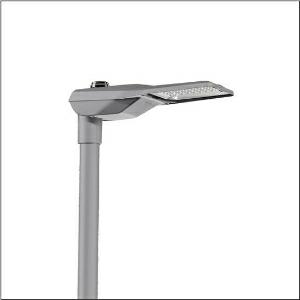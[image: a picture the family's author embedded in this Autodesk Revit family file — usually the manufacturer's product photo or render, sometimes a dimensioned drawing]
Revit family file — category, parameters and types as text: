
# Revit family: streetlight_sl_21_mini___p1_0a_5xe6a37n08gb_7347
name_source: partatom
category: Lighting Fixtures
units: mm (PartAtom-declared; Revit-internal decimal feet)

## family parameters
Cut with Voids When Loaded = No
Host = Face
Light Source = No
Part Type = Normal
Room Calculation Point = No
Round Connector Dimension = Use Diameter
Shared = No

## types (1)
- --- (1 x LED, 5940 lm, 40.4 W, 3000K)
    Apparent Load = 40 VA
    CIE Flux Codes = 21 50 90 100 100
    Color Rendering = 70
    Color Temperature = 3000K
    Default Elevation = 1800 mm
    Description = Streetlight SL 21 mini, mast luminaire, primary light control with lens, of PMMA, primary optical cover: cover, of toughened safety glass, transparent, light distribution: P1.0a, light emission: direct distribution, primary light characteristic: asymmetric, installation type: side-entry, LED, 3G 1.5mm², High Power LED, rated luminous flux: 5.940lm, luminous efficacy: 147lm/W, light colour: 730, colour temperature: 3000K, control gear: NEMA (7pin), control: overheat protection, pre-setting: linear dimming characteristic, constant luminous flux control, time-dependent luminous flux control, flexible luminous flux parameterisation, mains connection: 230..240V, AC, 50/60Hz, connection cable pre-assembled, cable length: 8,5m, wiring characteristics: H07RN-F, start of lifetime: 40W, end of service life: 41W, reduction: 19W, luminaire housing, of diecast aluminium (EN AC-44300), powder-coated, SITECO metallic grey (DB 702S), corrosivity category C5 high according to DIN EN ISO 12944, multi-level sealing system, sealing non-destructively replaceable, inclination adjustable: 0°, 5°, 10°, 15°, length: 628mm, width: 235mm, height: 110mm, spigot size: 42mm (side-entry), mounting height: 4..8m, protection rating (complete): IP66, insulation class (complete): insulation class I (protective earthing), certification: CE, ENEC, ENEC+, VDE, impact resistance: IK10, permissible operating ambient temperature for outdoor applications: -40..+50°C, standard-compliant lighting for roads and squares, packaging unit: 1 piece

Light Distribution: P1.0a
    Height = 110 mm
    Lamp = 1 x LED
    Lamp Light Flux = 5940 lm
    Lamp Power = 40.4 W
    Lamp count = 1
    Length = 625 mm
    Luminous efficacy = 147 lm/W
    Manufacturer = Siteco
    ModVariant = No
    Model = 5XE6A37N08GB
    Number of Poles = 1
    OnlyDefault = Yes
    Power Factor = 1
    Product Name = Streetlight SL 21 mini | P1.0a
    Product group = mast luminaire | pylon top
    ProductGroupID = 6100
    Protection Class = Protection class I
    Protection Degree = IP 66
    RLX_Detail_Level = 1
    RLX_Emergency_Light_Flux = 0 lm
    RLX_Emergency_Type = 0
    RLX_Emergency_Type_DB = No
    RlxData = <blob elided: 37017 chars, md5=7145a92a>
    Socket = socket
    Standby Power = 0 W
    System Light Flux = 5940 lm
    System Power = 40 W
    Type Comments = factory setting: luminous flux: 100 % | dim-lin: 254 | 812 mA
    Type Image = l_1294379.jpg
    URL = http://relux.com
    VarID = @adj_134213
    Voltage = 0 V
    Weight = 0.00 kg
    Width = 234 mm

## geometry (parser evidence)
native form markers: Blend x4, Sweep x11
no freeform markers — native parametric forms only
